# Revit family: Domotics-DomesticRanges-GEWISS-CHORUS_CLIMATE-THERMOSTAT_2M
name_source: partatom
category: Apparecchi elettrici
revit_build: Autodesk Revit 2016 (Build: 20161004_0715(x64)
units: mm (PartAtom-declared; Revit-internal decimal feet)

## family parameters
Condiviso = Sì
Host = Superficie
Mantenere orientamento annotazione = Sì
Punto di calcolo locali = Sì
Quota connettore circolare = Usa diametro
Taglio con vuoti quando caricato = Sì
Tipo di parte = Normale

## types (3) — shared parameters
Catalogue = DOMOTICS
Catalogue Range = CHORUS - DOMESTIC RANGE
Description. = Thermostat
Distanza_effettiva_x = 1500 mm  [stored 4.92126 ft]
Electrocod = 1434
IDF = 322caec2-5007-42a7-b20b-6fba1830d32a
IDT = 42d69dd9-f973-4988-8959-220bdb3ffa1b
Immagine tipo = GW14705.jpg
No. Chorus modules = 2
No. Chorus modules: = 2
Produttore = GEWISS S.p.A.
Prospetto di default = 1219 mm
SEO = Thermostat
Supply voltage = 230 V ac - 50/60 Hz
Technical sheet = https://www.gewiss.com
Temperature adjustment = From +5°C to +35°C
Tipo_ = Chorus Termostato_GENERICO : GW14705 Termostato 2M 230Vac 50/60Hz titanio
URL = https://www.gewiss.com
Version file RFA = 19.0
zero-valued in all types: Distanza_x

## per-type parameters (varying)
| type | Colour | Descrizione | EAN code | Modello |
| GW14705 - Thermostat, 2M 230V-50/60hz titanium | Titanium | THERMOSTAT, 2M 230VAC-50/60Hz TITANIUM | 8011564268692 | GW14705 |
| GW12705 - Thermostat 2M 230V-50/60hz black | Black | THERMOSTAT 2M 230VAC-50/60Hz BLACK | 8011564267466 | GW12705 |
| GW10705 - Thermostat 2M 230V-50/60hz white | White | THERMOSTAT 2M 230VAC-50/60Hz WHITE | 8011564263116 | GW10705 |

note: [stored X ft] marks values corroborated as IEEE doubles in the binary element streams (Revit-internal decimal feet)

## geometry (parser evidence)
native form markers: Sweep x2
no freeform markers — native parametric forms only
